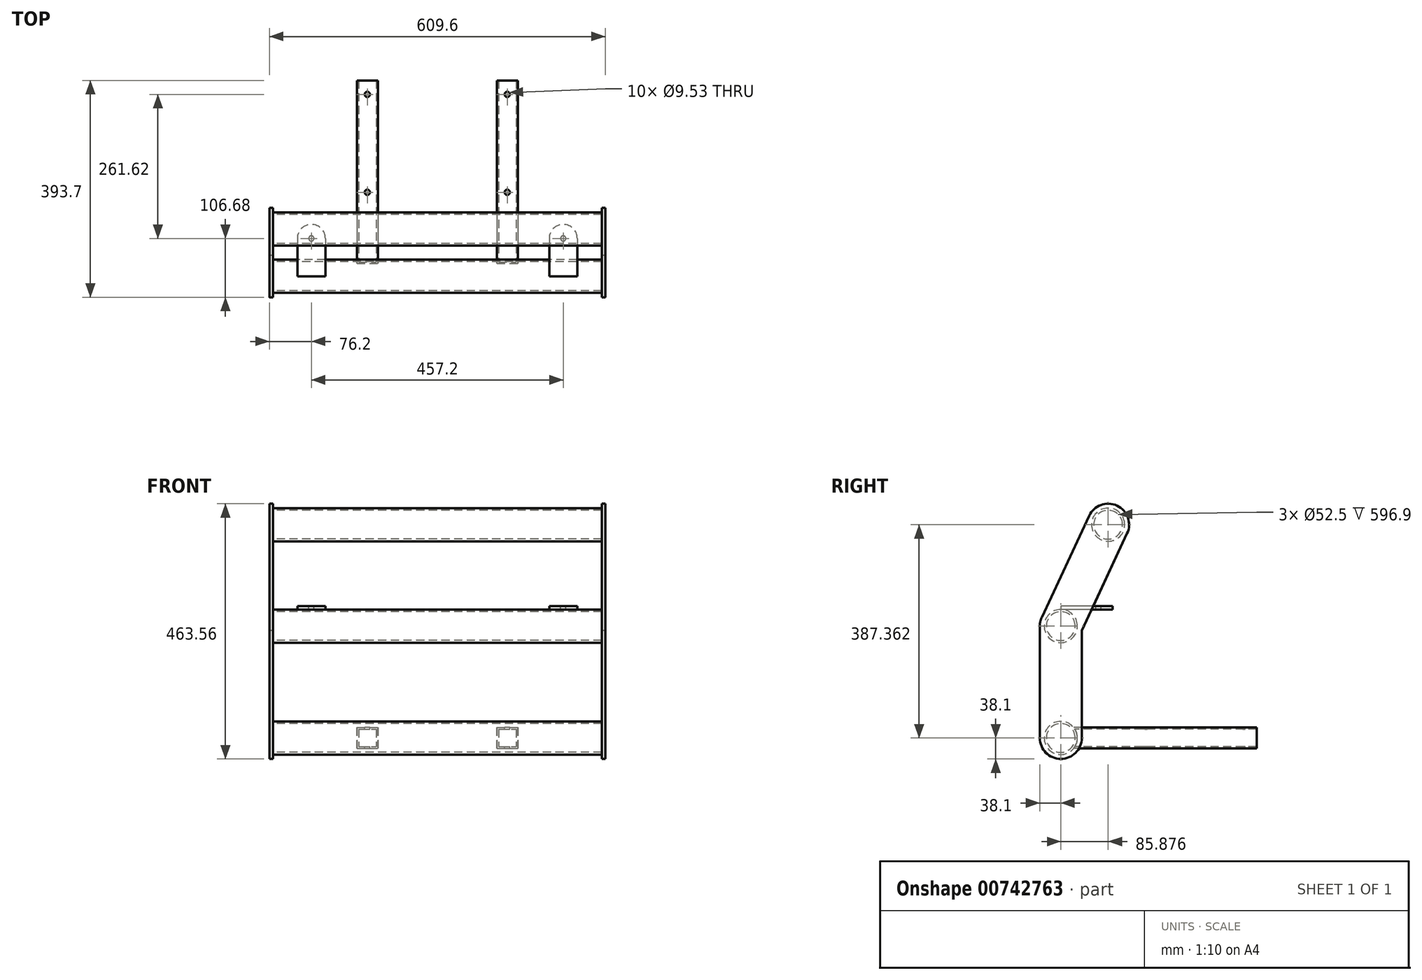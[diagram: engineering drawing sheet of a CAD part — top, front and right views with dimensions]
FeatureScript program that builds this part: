
annotation { "Feature Type Name" : "Feature", "Feature Type Description" : "" }
export const myFeature = defineFeature(function(context is Context, id is Id, definition is map)
    precondition{}
    {
        {
            var Q0;
            Q0=qCreatedBy(makeId("Right.planeOp"),FACE);
            var sketch = newSketch(context, id + "F0", { "sketchPlane" : qUnion([Q0])});
            skCircle(sketch, "E0", {"center": v(0, 0) * mm, "radius": 38.1 * mm});
            skCircle(sketch, "E1", {"center": v(85.88, 387.36) * mm, "radius": 38.1 * mm});
            skCircle(sketch, "E2", {"center": v(0, 203.2) * mm, "radius": 38.1 * mm});
            skLineSegment(sketch, "E3", {"start": v(120.4, 371.26) * mm, "end": v(34.53, 187.1) * mm});
            skLineSegment(sketch, "E4", {"start": v(51.35, 403.46) * mm, "end": v(-34.53, 219.3) * mm});
            skLineSegment(sketch, "E5", {"start": v(-38.1, 203.2) * mm, "end": v(-38.1, 0) * mm});
            skLineSegment(sketch, "E6", {"start": v(38.1, 203.2) * mm, "end": v(38.1, 0) * mm});
            skSolve(sketch);
        }
        {
            var Q0;
            Q0=qSketchRegion(id+"F0",true);
            extrude(context, id + "F1", {"entities" : qUnion([Q0]), "depth" : 609.6 * mm, "offsetDistance" : 25.4 * mm});
        }
        {
            var Q0;
            Q0=makeQuery(id+"F1.opExtrude","SWEPT_FACE",FACE,{"disambiguationData":[OSD([sQuery(id+"F0.wireOp",EDGE,"E5")])]});
            var sketch = newSketch(context, id + "F2", { "sketchPlane" : qUnion([Q0])});
            skLineSegment(sketch, "E7.bottom", {"start": v(6.35, 447.3) * mm, "end": v(603.25, 447.3) * mm});
            skLineSegment(sketch, "E7.top", {"start": v(6.35, -63.5) * mm, "end": v(603.25, -63.5) * mm});
            skLineSegment(sketch, "E7.left", {"start": v(6.35, 447.3) * mm, "end": v(6.35, -63.5) * mm});
            skLineSegment(sketch, "E7.right", {"start": v(603.25, 447.3) * mm, "end": v(603.25, -63.5) * mm});
            skSolve(sketch);
        }
        {
            var Q0;
            Q0=qSketchRegion(id+"F2",true);
            extrude(context, id + "F3", {"entities" : qUnion([Q0]), "operationType" : NewBodyOperationType.REMOVE, "endBound" : BoundingType.THROUGH_ALL, "oppositeDirection" : true, "depth" : 25.4 * mm, "offsetDistance" : 25.4 * mm});
        }
        {
            var Q0;
            Q0=makeQuery(id+"F3.boolean.opBoolean","COPY",FACE,{"derivedFrom":makeQuery(id+"F3.opExtrude","SWEPT_FACE",FACE,{"disambiguationData":[OSD([sQuery(id+"F2.wireOp",EDGE,"E7.left")])]})});
            var sketch = newSketch(context, id + "F4", { "sketchPlane" : qUnion([Q0])});
            skCircle(sketch, "E8", {"center": v(0, 0) * mm, "radius": 30.16 * mm});
            skCircle(sketch, "E9", {"center": v(0, 0) * mm, "radius": 26.25 * mm});
            skSolve(sketch);
        }
        {
            var Q0;
            Q0=qSketchRegion(id+"F4",true);
            extrude(context, id + "F5", {"entities" : qUnion([Q0]), "depth" : 596.9 * mm, "offsetDistance" : 25.4 * mm});
        }
        {
            var Q0;
            Q0=makeQuery(id+"F3.boolean.opBoolean","COPY",FACE,{"derivedFrom":makeQuery(id+"F3.opExtrude","SWEPT_FACE",FACE,{"disambiguationData":[OSD([sQuery(id+"F2.wireOp",EDGE,"E7.left")])]})});
            var sketch = newSketch(context, id + "F6", { "sketchPlane" : qUnion([Q0])});
            skCircle(sketch, "E10", {"center": v(0, 203.2) * mm, "radius": 30.16 * mm});
            skCircle(sketch, "E11", {"center": v(0, 203.2) * mm, "radius": 26.25 * mm});
            skSolve(sketch);
        }
        {
            var Q0;
            Q0=qSketchRegion(id+"F6",true);
            extrude(context, id + "F7", {"entities" : qUnion([Q0]), "depth" : 596.9 * mm, "offsetDistance" : 25.4 * mm});
        }
        {
            var Q0;
            Q0=makeQuery(id+"F3.boolean.opBoolean","COPY",FACE,{"derivedFrom":makeQuery(id+"F3.opExtrude","SWEPT_FACE",FACE,{"disambiguationData":[OSD([sQuery(id+"F2.wireOp",EDGE,"E7.left")])]})});
            var sketch = newSketch(context, id + "F8", { "sketchPlane" : qUnion([Q0])});
            skCircle(sketch, "E12", {"center": v(85.88, 387.36) * mm, "radius": 30.16 * mm});
            skCircle(sketch, "E13", {"center": v(85.88, 387.36) * mm, "radius": 26.25 * mm});
            skSolve(sketch);
        }
        {
            var Q0;
            Q0=qSketchRegion(id+"F8",true);
            extrude(context, id + "F9", {"entities" : qUnion([Q0]), "depth" : 596.9 * mm, "offsetDistance" : 25.4 * mm});
        }
        {
            var Q0;
            Q0=qCreatedBy(makeId("Front.planeOp"),FACE);
            var sketch = newSketch(context, id + "F10", { "sketchPlane" : qUnion([Q0])});
            skLineSegment(sketch, "E14.bottom", {"start": v(-95.25, 19.05) * mm, "end": v(-57.15, 19.05) * mm});
            skLineSegment(sketch, "E14.top", {"start": v(-95.25, -19.05) * mm, "end": v(-57.15, -19.05) * mm});
            skLineSegment(sketch, "E14.left", {"start": v(-95.25, 19.05) * mm, "end": v(-95.25, -19.05) * mm});
            skLineSegment(sketch, "E14.right", {"start": v(-57.15, 19.05) * mm, "end": v(-57.15, -19.05) * mm});
            skLineSegment(sketch, "E15.bottom", {"start": v(-92.07, 15.87) * mm, "end": v(-60.32, 15.87) * mm});
            skLineSegment(sketch, "E15.top", {"start": v(-92.07, -15.88) * mm, "end": v(-60.32, -15.88) * mm});
            skLineSegment(sketch, "E15.left", {"start": v(-92.07, 15.87) * mm, "end": v(-92.07, -15.88) * mm});
            skLineSegment(sketch, "E15.right", {"start": v(-60.32, 15.87) * mm, "end": v(-60.32, -15.88) * mm});
            skSolve(sketch);
        }
        {
            var Q0;
            Q0=qSketchRegion(id+"F10",true);
            extrude(context, id + "F11", {"entities" : qUnion([Q0]), "operationType" : NewBodyOperationType.ADD, "oppositeDirection" : true, "depth" : 355.6 * mm, "offsetDistance" : 25.4 * mm});
        }
        {
            var Q0;
            Q0=makeQuery(id+"F11.opExtrude","SWEPT_FACE",FACE,{"disambiguationData":[OSD([sQuery(id+"F10.wireOp",EDGE,"E14.right")])]});
            var sketch = newSketch(context, id + "F12", { "sketchPlane" : qUnion([Q0])});
            skCircle(sketch, "E16", {"center": v(0, 0) * mm, "radius": 30.16 * mm});
            skSolve(sketch);
        }
        {
            var Q0;
            Q0=qSketchRegion(id+"F12",true);
            extrude(context, id + "F13", {"entities" : qUnion([Q0]), "operationType" : NewBodyOperationType.REMOVE, "oppositeDirection" : true, "depth" : 38.1 * mm, "offsetDistance" : 25.4 * mm});
        }
        {
            var Q0;
            Q0=makeQuery(id+"F11.opExtrude","SWEPT_FACE",FACE,{"disambiguationData":[OSD([sQuery(id+"F10.wireOp",EDGE,"E14.bottom")])]});
            var sketch = newSketch(context, id + "F14", { "sketchPlane" : qUnion([Q0])});
            skCircle(sketch, "E17", {"center": v(-76.2, 330.2) * mm, "radius": 4.76 * mm});
            skCircle(sketch, "E18", {"center": v(-76.2, 152.4) * mm, "radius": 4.76 * mm});
            skSolve(sketch);
        }
        {
            var Q0;
            Q0=qSketchRegion(id+"F14",true);
            extrude(context, id + "F15", {"entities" : qUnion([Q0]), "operationType" : NewBodyOperationType.REMOVE, "endBound" : BoundingType.THROUGH_ALL, "oppositeDirection" : true, "depth" : 25.4 * mm, "offsetDistance" : 25.4 * mm});
        }
        {
            var Q0;
            Q0=makeQuery(id+"F11.opExtrude","SWEPT_BODY",BODY,{"disambiguationData":[OSD([sQuery(id+"F10.wireOp",EDGE,"E14.bottom"),sQuery(id+"F10.wireOp",EDGE,"E14.top"),sQuery(id+"F10.wireOp",EDGE,"E14.left"),sQuery(id+"F10.wireOp",EDGE,"E14.right"),sQuery(id+"F10.wireOp",EDGE,"E15.bottom"),sQuery(id+"F10.wireOp",EDGE,"E15.top"),sQuery(id+"F10.wireOp",EDGE,"E15.left"),sQuery(id+"F10.wireOp",EDGE,"E15.right")])]});
            transform(context, id + "F16", {"entities" : qUnion([Q0]), "transformType" : TransformType.TRANSLATION_3D, "dx" : 508 * mm, "dy" : 0 * mm, "dz" : 0 * mm, "makeCopy" : false});
        }
        {
            var Q0;
            Q0=qCreatedBy(makeId("Front.planeOp"),FACE);
            var sketch = newSketch(context, id + "F17", { "sketchPlane" : qUnion([Q0])});
            skLineSegment(sketch, "E19.bottom", {"start": v(50.8, 265.11) * mm, "end": v(101.6, 265.11) * mm});
            skLineSegment(sketch, "E19.top", {"start": v(50.8, 258.76) * mm, "end": v(101.6, 258.76) * mm});
            skLineSegment(sketch, "E19.left", {"start": v(50.8, 265.11) * mm, "end": v(50.8, 258.76) * mm});
            skLineSegment(sketch, "E19.right", {"start": v(101.6, 265.11) * mm, "end": v(101.6, 258.76) * mm});
            skSolve(sketch);
        }
        {
            var Q0;
            Q0=qSketchRegion(id+"F17",true);
            extrude(context, id + "F18", {"entities" : qUnion([Q0]), "oppositeDirection" : true, "depth" : 93.98 * mm, "offsetDistance" : 25.4 * mm});
        }
        {
            var Q0;
            Q0=makeQuery(id+"F18.opExtrude","CAP_EDGE",EDGE,{"disambiguationData":[OSD([sQuery(id+"F17.wireOp",EDGE,"E19.right")])],"isStart":false});
            var Q1;
            Q1=makeQuery(id+"F18.opExtrude","CAP_EDGE",EDGE,{"disambiguationData":[OSD([sQuery(id+"F17.wireOp",EDGE,"E19.left")])],"isStart":false});
            fillet(context, id + "F19", {"entities" : qUnion([Q0, Q1]), "radius" : 25.4 * mm, "tangentPropagation" : true, "allowEdgeOverflow" : false});
        }
        {
            var Q0;
            Q0=makeQuery(id+"F18.opExtrude","SWEPT_FACE",FACE,{"disambiguationData":[OSD([sQuery(id+"F17.wireOp",EDGE,"E19.bottom")])]});
            var sketch = newSketch(context, id + "F20", { "sketchPlane" : qUnion([Q0])});
            skCircle(sketch, "E20", {"center": v(76.2, 68.58) * mm, "radius": 4.76 * mm});
            skSolve(sketch);
        }
        {
            var Q0;
            Q0=qSketchRegion(id+"F20",true);
            extrude(context, id + "F21", {"entities" : qUnion([Q0]), "operationType" : NewBodyOperationType.REMOVE, "endBound" : BoundingType.THROUGH_ALL, "oppositeDirection" : true, "depth" : 25.4 * mm, "offsetDistance" : 25.4 * mm});
        }
        {
            var Q0;
            Q0=makeQuery(id+"F18.opExtrude","SWEPT_BODY",BODY,{"disambiguationData":[OSD([sQuery(id+"F17.wireOp",EDGE,"E19.bottom"),sQuery(id+"F17.wireOp",EDGE,"E19.top"),sQuery(id+"F17.wireOp",EDGE,"E19.left"),sQuery(id+"F17.wireOp",EDGE,"E19.right")])]});
            transform(context, id + "F22", {"entities" : qUnion([Q0]), "transformType" : TransformType.TRANSLATION_3D, "dx" : 457.2 * mm, "dy" : 0 * mm, "dz" : -25.4 * mm, "makeCopy" : true});
        }
        {
            var Q0;
            Q0=makeQuery(id+"F18.opExtrude","SWEPT_BODY",BODY,{"disambiguationData":[OSD([sQuery(id+"F17.wireOp",EDGE,"E19.bottom"),sQuery(id+"F17.wireOp",EDGE,"E19.top"),sQuery(id+"F17.wireOp",EDGE,"E19.left"),sQuery(id+"F17.wireOp",EDGE,"E19.right")])]});
            transform(context, id + "F23", {"entities" : qUnion([Q0]), "transformType" : TransformType.TRANSLATION_3D, "dx" : 0 * mm, "dy" : 0 * mm, "dz" : -25.4 * mm, "makeCopy" : false});
        }
        {
            var Q0;
            Q0=makeQuery(id+"F11.opExtrude","SWEPT_BODY",BODY,{"disambiguationData":[OSD([sQuery(id+"F10.wireOp",EDGE,"E14.bottom"),sQuery(id+"F10.wireOp",EDGE,"E14.top"),sQuery(id+"F10.wireOp",EDGE,"E14.left"),sQuery(id+"F10.wireOp",EDGE,"E14.right"),sQuery(id+"F10.wireOp",EDGE,"E15.bottom"),sQuery(id+"F10.wireOp",EDGE,"E15.top"),sQuery(id+"F10.wireOp",EDGE,"E15.left"),sQuery(id+"F10.wireOp",EDGE,"E15.right")])]});
            transform(context, id + "F24", {"entities" : qUnion([Q0]), "transformType" : TransformType.TRANSLATION_3D, "dx" : -254 * mm, "dy" : 0 * mm, "dz" : 0 * mm, "makeCopy" : true});
        }
    });
